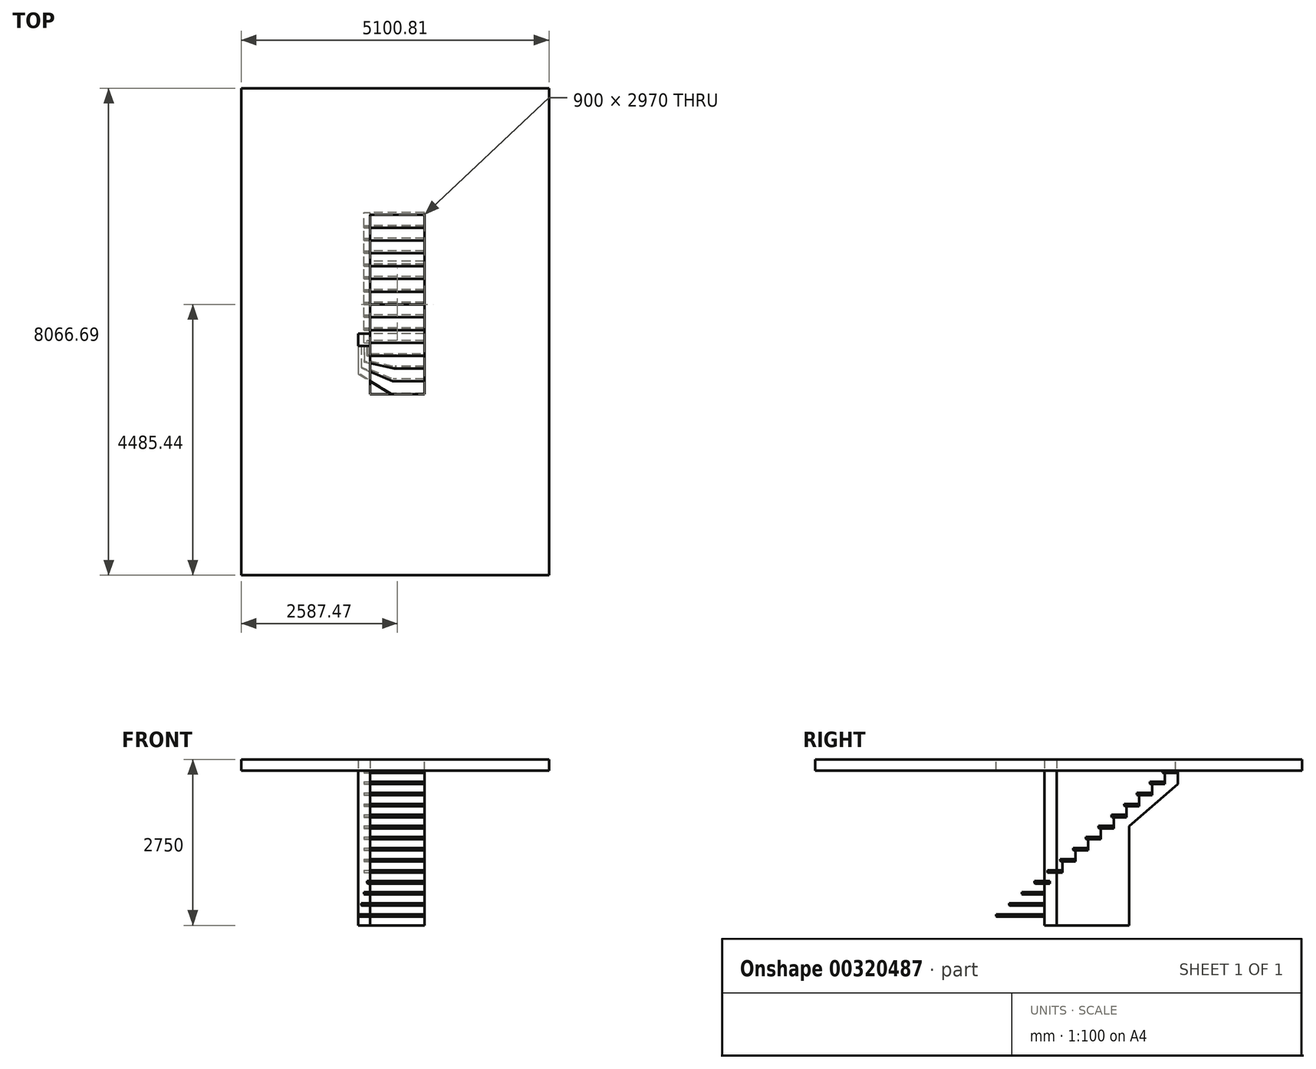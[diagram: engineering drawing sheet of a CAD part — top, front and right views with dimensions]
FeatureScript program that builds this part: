
annotation { "Feature Type Name" : "Feature", "Feature Type Description" : "" }
export const myFeature = defineFeature(function(context is Context, id is Id, definition is map)
    precondition{}
    {
        {
            var Q0;
            Q0=qCreatedBy(makeId("Top.planeOp"),FACE);
            var sketch = newSketch(context, id + "F0", { "sketchPlane" : qUnion([Q0])});
            skLineSegment(sketch, "E0.bottom", {"start": v(0, 2170) * mm, "end": v(-900, 2170) * mm});
            skLineSegment(sketch, "E0.top", {"start": v(0, -800) * mm, "end": v(-900, -800) * mm});
            skLineSegment(sketch, "E0.left", {"start": v(0, 2170) * mm, "end": v(0, -800) * mm});
            skLineSegment(sketch, "E0.right", {"start": v(-900, 2170) * mm, "end": v(-900, -800) * mm});
            skSolve(sketch);
        }
        {
            var Q0;
            Q0=qCreatedBy(makeId("Top.planeOp"),FACE);
            cPlane(context, id + "F1", {"entities" : qUnion([Q0]), "cplaneType" : CPlaneType.OFFSET, "offset" : 2750 * mm, "width" : 150 * mm, "height" : 150 * mm});
        }
        {
            var Q0;
            Q0=qCreatedBy(id+"F1.planeOp",FACE);
            var sketch = newSketch(context, id + "F2", { "sketchPlane" : qUnion([Q0])});
            skLineSegment(sketch, "E1.0", {"start": v(0, 2170) * mm, "end": v(-900, 2170) * mm});
            skLineSegment(sketch, "E1.1", {"start": v(-900, 2170) * mm, "end": v(-900, -800) * mm});
            skLineSegment(sketch, "E1.2", {"start": v(0, -800) * mm, "end": v(-900, -800) * mm});
            skLineSegment(sketch, "E1.3", {"start": v(0, 2170) * mm, "end": v(0, -800) * mm});
            skLineSegment(sketch, "E2.bottom", {"start": v(-3037.47, 4266.25) * mm, "end": v(2063.34, 4266.25) * mm});
            skLineSegment(sketch, "E2.top", {"start": v(-3037.47, -3800.44) * mm, "end": v(2063.34, -3800.44) * mm});
            skLineSegment(sketch, "E2.left", {"start": v(-3037.47, 4266.25) * mm, "end": v(-3037.47, -3800.44) * mm});
            skLineSegment(sketch, "E2.right", {"start": v(2063.34, 4266.25) * mm, "end": v(2063.34, -3800.44) * mm});
            skSolve(sketch);
        }
        {
            var Q0;
            Q0=makeQuery(id+"F2.imprint","IMPRINT",FACE,{"disambiguationData":[TD([[makeQuery(id+"F2.imprint","IMPRINT",EDGE,{"derivedFrom":sQuery(id+"F2.wireOp",EDGE,"E1.0")}),-1.0]])]});
            extrude(context, id + "F3", {"entities" : qUnion([Q0]), "oppositeDirection" : true, "depth" : 188 * mm});
        }
        {
            var Q0;
            Q0=qCreatedBy(makeId("Top.planeOp"),FACE);
            var sketch = newSketch(context, id + "F4", { "sketchPlane" : qUnion([Q0])});
            skPoint(sketch, "E3.0", {"position": v(0, 0) * mm});
            skLineSegment(sketch, "E4.0", {"start": v(-900, 2170) * mm, "end": v(-900, -800) * mm});
            skLineSegment(sketch, "E5.bottom", {"start": v(-900, 0) * mm, "end": v(-1100, 0) * mm});
            skLineSegment(sketch, "E5.top", {"start": v(-900, 200) * mm, "end": v(-1100, 200) * mm});
            skLineSegment(sketch, "E5.left", {"start": v(-900, 0) * mm, "end": v(-900, 200) * mm});
            skLineSegment(sketch, "E5.right", {"start": v(-1100, 0) * mm, "end": v(-1100, 200) * mm});
            skSolve(sketch);
        }
        {
            var Q0;
            Q0=makeQuery(id+"F4.imprint","IMPRINT",FACE,{"disambiguationData":[TD([[makeQuery(id+"F4.imprint","IMPRINT",EDGE,{"derivedFrom":sQuery(id+"F4.wireOp",EDGE,"E5.bottom")}),-1.0]])]});
            var Q1;
            Q1=qCreatedBy(id+"F1.planeOp",FACE);
            extrude(context, id + "F5", {"entities" : qUnion([Q0]), "endBound" : BoundingType.UP_TO_SURFACE, "endBoundEntityFace" : qUnion([Q1]), "depth" : 25 * mm});
        }
        {
            var Q0;
            Q0=qCreatedBy(makeId("Right.planeOp"),FACE);
            var Q1;
            Q1=sQuery(id+"F0.wireOp",VERTEX,"E0.right.end");
            cPlane(context, id + "F6", {"entities" : qUnion([Q0, Q1]), "cplaneType" : CPlaneType.PLANE_POINT, "offset" : 25 * mm, "width" : 150 * mm, "height" : 150 * mm});
        }
        {
            var Q0;
            Q0=qCreatedBy(id+"F6.planeOp",FACE);
            var sketch = newSketch(context, id + "F7", { "sketchPlane" : qUnion([Q0])});
            skLineSegment(sketch, "E6", {"start": v(-800, 0) * mm, "end": v(-800, 183) * mm});
            skLineSegment(sketch, "E7", {"start": v(-800, 183) * mm, "end": v(-588, 183) * mm});
            skLineSegment(sketch, "E8", {"start": v(-588, 183) * mm, "end": v(-588, 366) * mm});
            skLineSegment(sketch, "E9", {"start": v(-588, 366) * mm, "end": v(-376, 366) * mm});
            skLineSegment(sketch, "E10", {"start": v(-376, 366) * mm, "end": v(-376, 549) * mm});
            skLineSegment(sketch, "E11", {"start": v(-376, 549) * mm, "end": v(-164, 549) * mm});
            skLineSegment(sketch, "E12", {"start": v(-164, 549) * mm, "end": v(-164, 732) * mm});
            skLineSegment(sketch, "E13", {"start": v(-164, 732) * mm, "end": v(48, 732) * mm});
            skLineSegment(sketch, "E14", {"start": v(48, 732) * mm, "end": v(48, 915) * mm});
            skLineSegment(sketch, "E15", {"start": v(48, 915) * mm, "end": v(260, 915) * mm});
            skLineSegment(sketch, "E16", {"start": v(260, 915) * mm, "end": v(260, 1098) * mm});
            skLineSegment(sketch, "E17", {"start": v(260, 1098) * mm, "end": v(472, 1098) * mm});
            skLineSegment(sketch, "E18", {"start": v(472, 1098) * mm, "end": v(472, 1281) * mm});
            skLineSegment(sketch, "E19", {"start": v(472, 1281) * mm, "end": v(684, 1281) * mm});
            skLineSegment(sketch, "E20", {"start": v(684, 1281) * mm, "end": v(684, 1464) * mm});
            skLineSegment(sketch, "E21", {"start": v(684, 1464) * mm, "end": v(896, 1464) * mm});
            skLineSegment(sketch, "E22", {"start": v(896, 1464) * mm, "end": v(896, 1647) * mm});
            skLineSegment(sketch, "E23", {"start": v(896, 1647) * mm, "end": v(1108, 1647) * mm});
            skPoint(sketch, "E24.0", {"position": v(2170, 2750) * mm});
            skLineSegment(sketch, "E25", {"start": v(1108, 1647) * mm, "end": v(1108, 1830) * mm});
            skLineSegment(sketch, "E26", {"start": v(1108, 1830) * mm, "end": v(1320, 1830) * mm});
            skLineSegment(sketch, "E27", {"start": v(1320, 1830) * mm, "end": v(1320, 2013) * mm});
            skLineSegment(sketch, "E28", {"start": v(1320, 2013) * mm, "end": v(1532, 2013) * mm});
            skLineSegment(sketch, "E29", {"start": v(1532, 2013) * mm, "end": v(1532, 2196) * mm});
            skLineSegment(sketch, "E30", {"start": v(1532, 2196) * mm, "end": v(1744, 2196) * mm});
            skLineSegment(sketch, "E31", {"start": v(1744, 2196) * mm, "end": v(1744, 2379) * mm});
            skLineSegment(sketch, "E32", {"start": v(1744, 2379) * mm, "end": v(1956, 2379) * mm});
            skLineSegment(sketch, "E33", {"start": v(1956, 2379) * mm, "end": v(1956, 2562) * mm});
            skLineSegment(sketch, "E34", {"start": v(1956, 2562) * mm, "end": v(2168, 2562) * mm});
            skLineSegment(sketch, "E35", {"start": v(2168, 2562) * mm, "end": v(2168, 2745) * mm});
            skLineSegment(sketch, "E36", {"start": v(2168, 2745) * mm, "end": v(2380, 2745) * mm});
            skSolve(sketch);
        }
        {
            var Q0;
            Q0=qCreatedBy(id+"F6.planeOp",FACE);
            var sketch = newSketch(context, id + "F8", { "sketchPlane" : qUnion([Q0])});
            skLineSegment(sketch, "E37.0", {"start": v(2168, 2745) * mm, "end": v(2380, 2745) * mm});
            skLineSegment(sketch, "E37.1", {"start": v(1956, 2562) * mm, "end": v(2168, 2562) * mm});
            skLineSegment(sketch, "E37.2", {"start": v(1744, 2379) * mm, "end": v(1956, 2379) * mm});
            skLineSegment(sketch, "E37.3", {"start": v(1532, 2196) * mm, "end": v(1744, 2196) * mm});
            skLineSegment(sketch, "E37.4", {"start": v(1320, 2013) * mm, "end": v(1532, 2013) * mm});
            skLineSegment(sketch, "E37.5", {"start": v(1108, 1830) * mm, "end": v(1320, 1830) * mm});
            skLineSegment(sketch, "E37.6", {"start": v(896, 1647) * mm, "end": v(1108, 1647) * mm});
            skLineSegment(sketch, "E37.7", {"start": v(684, 1464) * mm, "end": v(896, 1464) * mm});
            skLineSegment(sketch, "E37.8", {"start": v(472, 1281) * mm, "end": v(684, 1281) * mm});
            skLineSegment(sketch, "E37.9", {"start": v(260, 1098) * mm, "end": v(472, 1098) * mm});
            skLineSegment(sketch, "E37.10", {"start": v(48, 915) * mm, "end": v(260, 915) * mm});
            skLineSegment(sketch, "E38.bottom", {"start": v(1956, 2562) * mm, "end": v(2206, 2562) * mm});
            skLineSegment(sketch, "E38.top", {"start": v(1956, 2522) * mm, "end": v(2206, 2522) * mm});
            skLineSegment(sketch, "E38.left", {"start": v(1956, 2562) * mm, "end": v(1956, 2522) * mm});
            skLineSegment(sketch, "E38.right", {"start": v(2206, 2562) * mm, "end": v(2206, 2522) * mm});
            skLineSegment(sketch, "E39.bottom", {"start": v(1744, 2379) * mm, "end": v(1994, 2379) * mm});
            skLineSegment(sketch, "E39.top", {"start": v(1744, 2339) * mm, "end": v(1994, 2339) * mm});
            skLineSegment(sketch, "E39.left", {"start": v(1744, 2379) * mm, "end": v(1744, 2339) * mm});
            skLineSegment(sketch, "E39.right", {"start": v(1994, 2379) * mm, "end": v(1994, 2339) * mm});
            skLineSegment(sketch, "E40.bottom", {"start": v(1532, 2196) * mm, "end": v(1782, 2196) * mm});
            skLineSegment(sketch, "E40.top", {"start": v(1532, 2156) * mm, "end": v(1782, 2156) * mm});
            skLineSegment(sketch, "E40.left", {"start": v(1532, 2196) * mm, "end": v(1532, 2156) * mm});
            skLineSegment(sketch, "E40.right", {"start": v(1782, 2196) * mm, "end": v(1782, 2156) * mm});
            skLineSegment(sketch, "E41.bottom", {"start": v(1320, 2013) * mm, "end": v(1570, 2013) * mm});
            skLineSegment(sketch, "E41.top", {"start": v(1320, 1973) * mm, "end": v(1570, 1973) * mm});
            skLineSegment(sketch, "E41.left", {"start": v(1320, 2013) * mm, "end": v(1320, 1973) * mm});
            skLineSegment(sketch, "E41.right", {"start": v(1570, 2013) * mm, "end": v(1570, 1973) * mm});
            skLineSegment(sketch, "E42.bottom", {"start": v(1108, 1830) * mm, "end": v(1358, 1830) * mm});
            skLineSegment(sketch, "E42.top", {"start": v(1108, 1790) * mm, "end": v(1358, 1790) * mm});
            skLineSegment(sketch, "E42.left", {"start": v(1108, 1830) * mm, "end": v(1108, 1790) * mm});
            skLineSegment(sketch, "E42.right", {"start": v(1358, 1830) * mm, "end": v(1358, 1790) * mm});
            skLineSegment(sketch, "E43.bottom", {"start": v(896, 1647) * mm, "end": v(1146, 1647) * mm});
            skLineSegment(sketch, "E43.top", {"start": v(896, 1607) * mm, "end": v(1146, 1607) * mm});
            skLineSegment(sketch, "E43.left", {"start": v(896, 1647) * mm, "end": v(896, 1607) * mm});
            skLineSegment(sketch, "E43.right", {"start": v(1146, 1647) * mm, "end": v(1146, 1607) * mm});
            skLineSegment(sketch, "E44.bottom", {"start": v(684, 1464) * mm, "end": v(934, 1464) * mm});
            skLineSegment(sketch, "E44.top", {"start": v(684, 1424) * mm, "end": v(934, 1424) * mm});
            skLineSegment(sketch, "E44.left", {"start": v(684, 1464) * mm, "end": v(684, 1424) * mm});
            skLineSegment(sketch, "E44.right", {"start": v(934, 1464) * mm, "end": v(934, 1424) * mm});
            skLineSegment(sketch, "E45.bottom", {"start": v(472, 1281) * mm, "end": v(722, 1281) * mm});
            skLineSegment(sketch, "E45.top", {"start": v(472, 1241) * mm, "end": v(722, 1241) * mm});
            skLineSegment(sketch, "E45.left", {"start": v(472, 1281) * mm, "end": v(472, 1241) * mm});
            skLineSegment(sketch, "E45.right", {"start": v(722, 1281) * mm, "end": v(722, 1241) * mm});
            skLineSegment(sketch, "E46.bottom", {"start": v(260, 1098) * mm, "end": v(510, 1098) * mm});
            skLineSegment(sketch, "E46.top", {"start": v(260, 1058) * mm, "end": v(510, 1058) * mm});
            skLineSegment(sketch, "E46.left", {"start": v(260, 1098) * mm, "end": v(260, 1058) * mm});
            skLineSegment(sketch, "E46.right", {"start": v(510, 1098) * mm, "end": v(510, 1058) * mm});
            skLineSegment(sketch, "E47.bottom", {"start": v(48, 915) * mm, "end": v(298, 915) * mm});
            skLineSegment(sketch, "E47.top", {"start": v(48, 875) * mm, "end": v(298, 875) * mm});
            skLineSegment(sketch, "E47.left", {"start": v(48, 915) * mm, "end": v(48, 875) * mm});
            skLineSegment(sketch, "E47.right", {"start": v(298, 915) * mm, "end": v(298, 875) * mm});
            skLineSegment(sketch, "E48.0", {"start": v(-164, 732) * mm, "end": v(48, 732) * mm});
            skLineSegment(sketch, "E49.bottom", {"start": v(-164, 732) * mm, "end": v(86, 732) * mm});
            skLineSegment(sketch, "E49.top", {"start": v(-164, 692) * mm, "end": v(86, 692) * mm});
            skLineSegment(sketch, "E49.left", {"start": v(-164, 732) * mm, "end": v(-164, 692) * mm});
            skLineSegment(sketch, "E49.right", {"start": v(86, 732) * mm, "end": v(86, 692) * mm});
            skSolve(sketch);
        }
        {
            var Q0;
            Q0=makeQuery(id+"F8.imprint","IMPRINT",FACE,{"disambiguationData":[TD([[makeQuery(id+"F8.imprint","IMPRINT",EDGE,{"derivedFrom":sQuery(id+"F8.wireOp",EDGE,"E38.top")}),1.0]])]});
            var Q1;
            Q1=makeQuery(id+"F8.imprint","IMPRINT",FACE,{"disambiguationData":[TD([[makeQuery(id+"F8.imprint","IMPRINT",EDGE,{"derivedFrom":sQuery(id+"F8.wireOp",EDGE,"E39.top")}),1.0]])]});
            var Q2;
            Q2=makeQuery(id+"F8.imprint","IMPRINT",FACE,{"disambiguationData":[TD([[makeQuery(id+"F8.imprint","IMPRINT",EDGE,{"derivedFrom":sQuery(id+"F8.wireOp",EDGE,"E40.top")}),1.0]])]});
            var Q3;
            Q3=makeQuery(id+"F8.imprint","IMPRINT",FACE,{"disambiguationData":[TD([[makeQuery(id+"F8.imprint","IMPRINT",EDGE,{"derivedFrom":sQuery(id+"F8.wireOp",EDGE,"E41.top")}),1.0]])]});
            var Q4;
            Q4=makeQuery(id+"F8.imprint","IMPRINT",FACE,{"disambiguationData":[TD([[makeQuery(id+"F8.imprint","IMPRINT",EDGE,{"derivedFrom":sQuery(id+"F8.wireOp",EDGE,"E42.top")}),1.0]])]});
            var Q5;
            Q5=makeQuery(id+"F8.imprint","IMPRINT",FACE,{"disambiguationData":[TD([[makeQuery(id+"F8.imprint","IMPRINT",EDGE,{"derivedFrom":sQuery(id+"F8.wireOp",EDGE,"E43.top")}),1.0]])]});
            var Q6;
            Q6=makeQuery(id+"F8.imprint","IMPRINT",FACE,{"disambiguationData":[TD([[makeQuery(id+"F8.imprint","IMPRINT",EDGE,{"derivedFrom":sQuery(id+"F8.wireOp",EDGE,"E44.top")}),1.0]])]});
            var Q7;
            Q7=makeQuery(id+"F8.imprint","IMPRINT",FACE,{"disambiguationData":[TD([[makeQuery(id+"F8.imprint","IMPRINT",EDGE,{"derivedFrom":sQuery(id+"F8.wireOp",EDGE,"E45.top")}),1.0]])]});
            var Q8;
            Q8=makeQuery(id+"F8.imprint","IMPRINT",FACE,{"disambiguationData":[TD([[makeQuery(id+"F8.imprint","IMPRINT",EDGE,{"derivedFrom":sQuery(id+"F8.wireOp",EDGE,"E46.top")}),1.0]])]});
            var Q9;
            Q9=makeQuery(id+"F8.imprint","IMPRINT",FACE,{"disambiguationData":[TD([[makeQuery(id+"F8.imprint","IMPRINT",EDGE,{"derivedFrom":sQuery(id+"F8.wireOp",EDGE,"E47.top")}),1.0]])]});
            var Q10;
            Q10=makeQuery(id+"F8.imprint","IMPRINT",FACE,{"disambiguationData":[TD([[makeQuery(id+"F8.imprint","IMPRINT",EDGE,{"derivedFrom":sQuery(id+"F8.wireOp",EDGE,"E49.top")}),1.0]])]});
            var Q11;
            Q11=qCreatedBy(makeId("Right.planeOp"),FACE);
            extrude(context, id + "F9", {"entities" : qUnion([Q0, Q1, Q2, Q3, Q4, Q5, Q6, Q7, Q8, Q9, Q10]), "endBound" : BoundingType.UP_TO_SURFACE, "endBoundEntityFace" : qUnion([Q11]), "depth" : 25 * mm});
        }
        {
            var Q0;
            Q0=makeQuery(id+"F9.opExtrude","CAP_FACE",FACE,{"disambiguationData":[OSD([sQuery(id+"F8.wireOp",EDGE,"E38.bottom"),sQuery(id+"F8.wireOp",EDGE,"E38.top"),sQuery(id+"F8.wireOp",EDGE,"E38.left"),sQuery(id+"F8.wireOp",EDGE,"E38.right")])],"isStart":true});
            var Q1;
            Q1=makeQuery(id+"F9.opExtrude","CAP_FACE",FACE,{"disambiguationData":[OSD([sQuery(id+"F8.wireOp",EDGE,"E39.bottom"),sQuery(id+"F8.wireOp",EDGE,"E39.top"),sQuery(id+"F8.wireOp",EDGE,"E39.left"),sQuery(id+"F8.wireOp",EDGE,"E39.right")])],"isStart":true});
            var Q2;
            Q2=makeQuery(id+"F9.opExtrude","CAP_FACE",FACE,{"disambiguationData":[OSD([sQuery(id+"F8.wireOp",EDGE,"E40.bottom"),sQuery(id+"F8.wireOp",EDGE,"E40.top"),sQuery(id+"F8.wireOp",EDGE,"E40.left"),sQuery(id+"F8.wireOp",EDGE,"E40.right")])],"isStart":true});
            var Q3;
            Q3=makeQuery(id+"F9.opExtrude","CAP_FACE",FACE,{"disambiguationData":[OSD([sQuery(id+"F8.wireOp",EDGE,"E41.bottom"),sQuery(id+"F8.wireOp",EDGE,"E41.top"),sQuery(id+"F8.wireOp",EDGE,"E41.left"),sQuery(id+"F8.wireOp",EDGE,"E41.right")])],"isStart":true});
            var Q4;
            Q4=makeQuery(id+"F9.opExtrude","CAP_FACE",FACE,{"disambiguationData":[OSD([sQuery(id+"F8.wireOp",EDGE,"E42.bottom"),sQuery(id+"F8.wireOp",EDGE,"E42.top"),sQuery(id+"F8.wireOp",EDGE,"E42.left"),sQuery(id+"F8.wireOp",EDGE,"E42.right")])],"isStart":true});
            var Q5;
            Q5=makeQuery(id+"F9.opExtrude","CAP_FACE",FACE,{"disambiguationData":[OSD([sQuery(id+"F8.wireOp",EDGE,"E43.bottom"),sQuery(id+"F8.wireOp",EDGE,"E43.top"),sQuery(id+"F8.wireOp",EDGE,"E43.left"),sQuery(id+"F8.wireOp",EDGE,"E43.right")])],"isStart":true});
            var Q6;
            Q6=makeQuery(id+"F9.opExtrude","CAP_FACE",FACE,{"disambiguationData":[OSD([sQuery(id+"F8.wireOp",EDGE,"E44.bottom"),sQuery(id+"F8.wireOp",EDGE,"E44.top"),sQuery(id+"F8.wireOp",EDGE,"E44.left"),sQuery(id+"F8.wireOp",EDGE,"E44.right")])],"isStart":true});
            var Q7;
            Q7=makeQuery(id+"F9.opExtrude","CAP_FACE",FACE,{"disambiguationData":[OSD([sQuery(id+"F8.wireOp",EDGE,"E45.bottom"),sQuery(id+"F8.wireOp",EDGE,"E45.top"),sQuery(id+"F8.wireOp",EDGE,"E45.left"),sQuery(id+"F8.wireOp",EDGE,"E45.right")])],"isStart":true});
            var Q8;
            Q8=makeQuery(id+"F9.opExtrude","CAP_FACE",FACE,{"disambiguationData":[OSD([sQuery(id+"F8.wireOp",EDGE,"E46.bottom"),sQuery(id+"F8.wireOp",EDGE,"E46.top"),sQuery(id+"F8.wireOp",EDGE,"E46.left"),sQuery(id+"F8.wireOp",EDGE,"E46.right")])],"isStart":true});
            var Q9;
            Q9=makeQuery(id+"F9.opExtrude","CAP_FACE",FACE,{"disambiguationData":[OSD([sQuery(id+"F8.wireOp",EDGE,"E47.bottom"),sQuery(id+"F8.wireOp",EDGE,"E47.top"),sQuery(id+"F8.wireOp",EDGE,"E47.left"),sQuery(id+"F8.wireOp",EDGE,"E47.right")])],"isStart":true});
            extrude(context, id + "F10", {"entities" : qUnion([Q0, Q1, Q2, Q3, Q4, Q5, Q6, Q7, Q8, Q9]), "depth" : 100 * mm});
        }
        {
            var Q0;
            Q0=qCreatedBy(id+"F6.planeOp",FACE);
            var sketch = newSketch(context, id + "F11", { "sketchPlane" : qUnion([Q0])});
            skLineSegment(sketch, "E50.0", {"start": v(298, 915) * mm, "end": v(298, 875) * mm});
            skLineSegment(sketch, "E50.1", {"start": v(510, 1098) * mm, "end": v(510, 1058) * mm});
            skLineSegment(sketch, "E50.2", {"start": v(722, 1281) * mm, "end": v(722, 1241) * mm});
            skLineSegment(sketch, "E50.3", {"start": v(934, 1464) * mm, "end": v(934, 1424) * mm});
            skLineSegment(sketch, "E50.4", {"start": v(1146, 1647) * mm, "end": v(1146, 1607) * mm});
            skLineSegment(sketch, "E50.5", {"start": v(1358, 1830) * mm, "end": v(1358, 1790) * mm});
            skLineSegment(sketch, "E50.6", {"start": v(1570, 2013) * mm, "end": v(1570, 1973) * mm});
            skLineSegment(sketch, "E50.7", {"start": v(1782, 2196) * mm, "end": v(1782, 2156) * mm});
            skLineSegment(sketch, "E50.8", {"start": v(1994, 2379) * mm, "end": v(1994, 2339) * mm});
            skLineSegment(sketch, "E50.9", {"start": v(2206, 2562) * mm, "end": v(2206, 2522) * mm});
            skLineSegment(sketch, "E51", {"start": v(298, 915) * mm, "end": v(298, 1058) * mm});
            skLineSegment(sketch, "E52", {"start": v(298, 1058) * mm, "end": v(510, 1058) * mm});
            skLineSegment(sketch, "E53", {"start": v(510, 1098) * mm, "end": v(510, 1241) * mm});
            skLineSegment(sketch, "E54", {"start": v(510, 1241) * mm, "end": v(722, 1241) * mm});
            skLineSegment(sketch, "E55", {"start": v(722, 1281) * mm, "end": v(722, 1424) * mm});
            skLineSegment(sketch, "E56", {"start": v(722, 1424) * mm, "end": v(934, 1424) * mm});
            skLineSegment(sketch, "E57", {"start": v(934, 1464) * mm, "end": v(934, 1607) * mm});
            skLineSegment(sketch, "E58", {"start": v(934, 1607) * mm, "end": v(1146, 1607) * mm});
            skLineSegment(sketch, "E59", {"start": v(1146, 1647) * mm, "end": v(1146, 1790) * mm});
            skLineSegment(sketch, "E60", {"start": v(1146, 1790) * mm, "end": v(1358, 1790) * mm});
            skLineSegment(sketch, "E61", {"start": v(1358, 1830) * mm, "end": v(1358, 1973) * mm});
            skLineSegment(sketch, "E62", {"start": v(1358, 1973) * mm, "end": v(1570, 1973) * mm});
            skLineSegment(sketch, "E63", {"start": v(1570, 2013) * mm, "end": v(1570, 2156) * mm});
            skLineSegment(sketch, "E64", {"start": v(1570, 2156) * mm, "end": v(1782, 2156) * mm});
            skLineSegment(sketch, "E65", {"start": v(1782, 2196) * mm, "end": v(1782, 2339) * mm});
            skLineSegment(sketch, "E66", {"start": v(1782, 2339) * mm, "end": v(1994, 2339) * mm});
            skLineSegment(sketch, "E67", {"start": v(1994, 2379) * mm, "end": v(1994, 2522) * mm});
            skLineSegment(sketch, "E68", {"start": v(1994, 2522) * mm, "end": v(2206, 2522) * mm});
            skPoint(sketch, "E69.0", {"position": v(200, 875) * mm});
            skLineSegment(sketch, "E70", {"start": v(298, 875) * mm, "end": v(200, 875) * mm});
            skLineSegment(sketch, "E71", {"start": v(200, 0) * mm, "end": v(1400, 0) * mm});
            skLineSegment(sketch, "E72", {"start": v(1400, 0) * mm, "end": v(1400, 1973) * mm});
            skLineSegment(sketch, "E73", {"start": v(200, 875) * mm, "end": v(200, 0) * mm});
            skLineSegment(sketch, "E74", {"start": v(2206, 2522) * mm, "end": v(2206, 2339) * mm});
            skLineSegment(sketch, "E75", {"start": v(1146, 1607) * mm, "end": v(1146, 1424) * mm});
            skLineSegment(sketch, "E76", {"start": v(1146, 1424) * mm, "end": v(2206, 2339) * mm});
            skSolve(sketch);
        }
        {
            var Q0;
            Q0=makeQuery(id+"F11.imprint","IMPRINT",FACE,{"disambiguationData":[TD([[makeQuery(id+"F11.imprint","IMPRINT",EDGE,{"derivedFrom":sQuery(id+"F11.wireOp",EDGE,"E50.0")}),1.0]])]});
            var Q1;
            Q1=makeQuery(id+"F11.imprint","IMPRINT",FACE,{"disambiguationData":[TD([[makeQuery(id+"F11.imprint","IMPRINT",EDGE,{"derivedFrom":sQuery(id+"F11.wireOp",EDGE,"E50.4")}),1.0]])]});
            var Q2;
            {var subQ0=sQuery(id+"F11.wireOp",EDGE,"E50.6");Q2=makeQuery(id+"F11.imprint","IMPRINT",FACE,{"disambiguationData":[TD([[makeQuery(id+"F11.imprint","IMPRINT",EDGE,{"derivedFrom":subQ0}),1.0]])]});}
            var Q3;
            Q3=qCreatedBy(makeId("Right.planeOp"),FACE);
            extrude(context, id + "F12", {"entities" : qUnion([Q0, Q1, Q2]), "endBound" : BoundingType.UP_TO_SURFACE, "endBoundEntityFace" : qUnion([Q3]), "depth" : 25 * mm});
        }
        {
            var Q0;
            Q0=makeQuery(id+"F9.opExtrude","CAP_FACE",FACE,{"disambiguationData":[OSD([sQuery(id+"F8.wireOp",EDGE,"E49.bottom"),sQuery(id+"F8.wireOp",EDGE,"E49.top"),sQuery(id+"F8.wireOp",EDGE,"E49.left"),sQuery(id+"F8.wireOp",EDGE,"E49.right")])],"isStart":true});
            extrude(context, id + "F13", {"entities" : qUnion([Q0]), "depth" : 50 * mm});
        }
        {
            var Q0;
            Q0=qCreatedBy(makeId("Top.planeOp"),FACE);
            var Q1;
            Q1=sQuery(id+"F7.wireOp",VERTEX,"E11.start");
            cPlane(context, id + "F14", {"entities" : qUnion([Q0, Q1]), "cplaneType" : CPlaneType.PLANE_POINT, "offset" : 25 * mm, "width" : 150 * mm, "height" : 150 * mm});
        }
        {
            var Q0;
            Q0=qCreatedBy(makeId("Top.planeOp"),FACE);
            var Q1;
            Q1=sQuery(id+"F7.wireOp",VERTEX,"E9.start");
            cPlane(context, id + "F15", {"entities" : qUnion([Q0, Q1]), "cplaneType" : CPlaneType.PLANE_POINT, "offset" : 25 * mm, "width" : 150 * mm, "height" : 150 * mm});
        }
        {
            var Q0;
            Q0=qCreatedBy(makeId("Top.planeOp"),FACE);
            var Q1;
            Q1=sQuery(id+"F7.wireOp",VERTEX,"E7.start");
            cPlane(context, id + "F16", {"entities" : qUnion([Q0, Q1]), "cplaneType" : CPlaneType.PLANE_POINT, "offset" : 25 * mm, "width" : 150 * mm, "height" : 150 * mm});
        }
        {
            var Q0;
            Q0=qCreatedBy(id+"F14.planeOp",FACE);
            var sketch = newSketch(context, id + "F17", { "sketchPlane" : qUnion([Q0])});
            skPoint(sketch, "E77.0", {"position": v(-900, -376) * mm});
            skLineSegment(sketch, "E78.bottom", {"start": v(-500, -376) * mm, "end": v(0, -376) * mm});
            skLineSegment(sketch, "E78.top", {"start": v(-900, -126) * mm, "end": v(0, -126) * mm});
            skLineSegment(sketch, "E78.right", {"start": v(0, -376) * mm, "end": v(0, -126) * mm});
            skLineSegment(sketch, "E79", {"start": v(-1000, -126) * mm, "end": v(-1000, -266) * mm});
            skLineSegment(sketch, "E80", {"start": v(-1000, -266) * mm, "end": v(-500, -376) * mm});
            skLineSegment(sketch, "E81.0", {"start": v(-900, 0) * mm, "end": v(-1000, 0) * mm});
            skLineSegment(sketch, "E82", {"start": v(-900, -126) * mm, "end": v(-900, 0) * mm});
            skLineSegment(sketch, "E83", {"start": v(-1000, -126) * mm, "end": v(-1000, 0) * mm});
            skPoint(sketch, "E84.orphan", {"position": v(-1100, 0) * mm});
            skSolve(sketch);
        }
        {
            var Q0;
            Q0=makeQuery(id+"F17.imprint","IMPRINT",FACE,{"disambiguationData":[TD([[makeQuery(id+"F17.imprint","IMPRINT",EDGE,{"derivedFrom":sQuery(id+"F17.wireOp",EDGE,"E78.bottom")}),1.0]])]});
            extrude(context, id + "F18", {"entities" : qUnion([Q0]), "oppositeDirection" : true, "depth" : 40 * mm});
        }
        {
            var Q0;
            Q0=qCreatedBy(id+"F15.planeOp",FACE);
            var sketch = newSketch(context, id + "F19", { "sketchPlane" : qUnion([Q0])});
            skPoint(sketch, "E85.0", {"position": v(-900, -588) * mm});
            skLineSegment(sketch, "E86", {"start": v(-525, -588) * mm, "end": v(0, -588) * mm});
            skLineSegment(sketch, "E87", {"start": v(0, -588) * mm, "end": v(0, -338) * mm});
            skPoint(sketch, "E88", {"position": v(-525, -588) * mm});
            skPoint(sketch, "E89", {"position": v(-1000, -226) * mm});
            skLineSegment(sketch, "E90", {"start": v(0, -338) * mm, "end": v(-490.9, -338) * mm});
            skLineSegment(sketch, "E91", {"start": v(-900, -248) * mm, "end": v(-490.9, -338) * mm});
            skPoint(sketch, "E92.orphan", {"position": v(-1000, -266) * mm});
            skLineSegment(sketch, "E93", {"start": v(-1050, -226) * mm, "end": v(-1050, -366) * mm});
            skLineSegment(sketch, "E94", {"start": v(-1050, -366) * mm, "end": v(-525, -588) * mm});
            skLineSegment(sketch, "E95.0", {"start": v(-900, 0) * mm, "end": v(-1050, 0) * mm});
            skLineSegment(sketch, "E96", {"start": v(-900, 0) * mm, "end": v(-900, -248) * mm});
            skLineSegment(sketch, "E97", {"start": v(-1050, -226) * mm, "end": v(-1050, 0) * mm});
            skPoint(sketch, "E98.orphan", {"position": v(-1100, 0) * mm});
            skSolve(sketch);
        }
        {
            var Q0;
            Q0=makeQuery(id+"F19.imprint","IMPRINT",FACE,{"disambiguationData":[TD([[makeQuery(id+"F19.imprint","IMPRINT",EDGE,{"derivedFrom":sQuery(id+"F19.wireOp",EDGE,"E86")}),1.0]])]});
            extrude(context, id + "F20", {"entities" : qUnion([Q0]), "oppositeDirection" : true, "depth" : 40 * mm});
        }
        {
            var Q0;
            Q0=qCreatedBy(id+"F16.planeOp",FACE);
            var sketch = newSketch(context, id + "F21", { "sketchPlane" : qUnion([Q0])});
            skPoint(sketch, "E99.0", {"position": v(-900, -800) * mm});
            skLineSegment(sketch, "E100", {"start": v(-550, -800) * mm, "end": v(0, -800) * mm});
            skLineSegment(sketch, "E101", {"start": v(0, -800) * mm, "end": v(0, -550) * mm});
            skLineSegment(sketch, "E102", {"start": v(0, -550) * mm, "end": v(-520.27, -550) * mm});
            skPoint(sketch, "E103", {"position": v(-550, -800) * mm});
            skPoint(sketch, "E104", {"position": v(-1050, -326) * mm});
            skLineSegment(sketch, "E105", {"start": v(-900, -389.43) * mm, "end": v(-520.27, -550) * mm});
            skLineSegment(sketch, "E106.0", {"start": v(-900, 0) * mm, "end": v(-1100, 0) * mm});
            skLineSegment(sketch, "E107", {"start": v(-900, 0) * mm, "end": v(-900, -389.43) * mm});
            skLineSegment(sketch, "E108", {"start": v(-900, -389.43) * mm, "end": v(-900, 0) * mm});
            skLineSegment(sketch, "E109", {"start": v(-1100, -326) * mm, "end": v(-1100, -466) * mm});
            skPoint(sketch, "E110.orphan", {"position": v(-1050, -366) * mm});
            skPoint(sketch, "E111.0.end.orphan", {"position": v(-1050, 0) * mm});
            skLineSegment(sketch, "E112", {"start": v(-1100, 0) * mm, "end": v(-1100, -326) * mm});
            skLineSegment(sketch, "E113", {"start": v(-1100, -466) * mm, "end": v(-550, -800) * mm});
            skSolve(sketch);
        }
        {
            var Q0;
            Q0=makeQuery(id+"F21.imprint","IMPRINT",FACE,{"disambiguationData":[TD([[makeQuery(id+"F21.imprint","IMPRINT",EDGE,{"derivedFrom":sQuery(id+"F21.wireOp",EDGE,"E100")}),1.0]])]});
            extrude(context, id + "F22", {"entities" : qUnion([Q0]), "oppositeDirection" : true, "depth" : 40 * mm});
        }
        {
            var Q0;
            Q0=makeQuery(id+"F22.opExtrude","CAP_FACE",FACE,{"disambiguationData":[OSD([sQuery(id+"F21.wireOp",EDGE,"E100"),sQuery(id+"F21.wireOp",EDGE,"E101"),sQuery(id+"F21.wireOp",EDGE,"E102"),sQuery(id+"F21.wireOp",EDGE,"E105"),sQuery(id+"F21.wireOp",EDGE,"E106.0"),sQuery(id+"F21.wireOp",EDGE,"E108"),sQuery(id+"F21.wireOp",EDGE,"E109"),sQuery(id+"F21.wireOp",EDGE,"E112"),sQuery(id+"F21.wireOp",EDGE,"E113")])],"isStart":false});
            var sketch = newSketch(context, id + "F23", { "sketchPlane" : qUnion([Q0])});
            skLineSegment(sketch, "E114.0", {"start": v(-538.8, 760) * mm, "end": v(0, 760) * mm});
            skLineSegment(sketch, "E114.1", {"start": v(-1060, 443.5) * mm, "end": v(-538.8, 760) * mm});
            skLineSegment(sketch, "E114.2", {"start": v(-1060, 0) * mm, "end": v(-1060, 443.5) * mm});
            skSolve(sketch);
        }
        {
            var Q0;
            Q0=sQuery(id+"F23.wireOp",EDGE,"E114.2");
            var Q1;
            Q1=sQuery(id+"F23.wireOp",EDGE,"E114.1");
            var Q2;
            Q2=sQuery(id+"F23.wireOp",EDGE,"E114.0");
            var Q3;
            Q3=makeQuery(id+"F5.opExtrude","CAP_FACE",FACE,{"disambiguationData":[OSD([sQuery(id+"F4.wireOp",EDGE,"E5.bottom"),sQuery(id+"F4.wireOp",EDGE,"E5.top"),sQuery(id+"F4.wireOp",EDGE,"E5.left"),sQuery(id+"F4.wireOp",EDGE,"E5.right")])],"isStart":true});
            extrude(context, id + "F24", {"bodyType" : ToolBodyType.SURFACE, "surfaceEntities" : qUnion([Q0, Q1, Q2]), "endBound" : BoundingType.UP_TO_SURFACE, "endBoundEntityFace" : qUnion([Q3]), "depth" : 25 * mm});
        }
        {
            var Q0;
            Q0=makeQuery(id+"F20.opExtrude","CAP_FACE",FACE,{"disambiguationData":[OSD([sQuery(id+"F19.wireOp",EDGE,"E86"),sQuery(id+"F19.wireOp",EDGE,"E87"),sQuery(id+"F19.wireOp",EDGE,"E90"),sQuery(id+"F19.wireOp",EDGE,"E91"),sQuery(id+"F19.wireOp",EDGE,"E93"),sQuery(id+"F19.wireOp",EDGE,"E94"),sQuery(id+"F19.wireOp",EDGE,"E95.0"),sQuery(id+"F19.wireOp",EDGE,"E96"),sQuery(id+"F19.wireOp",EDGE,"E97")])],"isStart":false});
            var sketch = newSketch(context, id + "F25", { "sketchPlane" : qUnion([Q0])});
            skLineSegment(sketch, "E115.0", {"start": v(-1010, 339.49) * mm, "end": v(-1010, 0) * mm});
            skLineSegment(sketch, "E115.1", {"start": v(-1010, 339.49) * mm, "end": v(-516.9, 548) * mm});
            skLineSegment(sketch, "E115.2", {"start": v(-516.9, 548) * mm, "end": v(0, 548) * mm});
            skSolve(sketch);
        }
        {
            var Q0;
            Q0=sQuery(id+"F25.wireOp",EDGE,"E115.0");
            var Q1;
            Q1=sQuery(id+"F25.wireOp",EDGE,"E115.1");
            var Q2;
            Q2=sQuery(id+"F25.wireOp",EDGE,"E115.2");
            var Q3;
            Q3=makeQuery(id+"F22.opExtrude","CAP_FACE",FACE,{"disambiguationData":[OSD([sQuery(id+"F21.wireOp",EDGE,"E100"),sQuery(id+"F21.wireOp",EDGE,"E101"),sQuery(id+"F21.wireOp",EDGE,"E102"),sQuery(id+"F21.wireOp",EDGE,"E105"),sQuery(id+"F21.wireOp",EDGE,"E106.0"),sQuery(id+"F21.wireOp",EDGE,"E108"),sQuery(id+"F21.wireOp",EDGE,"E109"),sQuery(id+"F21.wireOp",EDGE,"E112"),sQuery(id+"F21.wireOp",EDGE,"E113")])],"isStart":true});
            extrude(context, id + "F26", {"bodyType" : ToolBodyType.SURFACE, "surfaceEntities" : qUnion([Q0, Q1, Q2]), "endBound" : BoundingType.UP_TO_SURFACE, "endBoundEntityFace" : qUnion([Q3]), "depth" : 25 * mm});
        }
        {
            var Q0;
            Q0=makeQuery(id+"F18.opExtrude","CAP_FACE",FACE,{"disambiguationData":[OSD([sQuery(id+"F17.wireOp",EDGE,"E78.bottom"),sQuery(id+"F17.wireOp",EDGE,"E78.top"),sQuery(id+"F17.wireOp",EDGE,"E78.right"),sQuery(id+"F17.wireOp",EDGE,"E79"),sQuery(id+"F17.wireOp",EDGE,"E80"),sQuery(id+"F17.wireOp",EDGE,"E81.0"),sQuery(id+"F17.wireOp",EDGE,"E82"),sQuery(id+"F17.wireOp",EDGE,"E83")])],"isStart":false});
            var sketch = newSketch(context, id + "F27", { "sketchPlane" : qUnion([Q0])});
            skLineSegment(sketch, "E116.0", {"start": v(-960, 233.84) * mm, "end": v(-960, 0) * mm});
            skLineSegment(sketch, "E116.1", {"start": v(-960, 233.84) * mm, "end": v(-495.65, 336) * mm});
            skLineSegment(sketch, "E116.2", {"start": v(-495.65, 336) * mm, "end": v(0, 336) * mm});
            skSolve(sketch);
        }
        {
            var Q0;
            Q0=sQuery(id+"F27.wireOp",EDGE,"E116.0");
            var Q1;
            Q1=sQuery(id+"F27.wireOp",EDGE,"E116.1");
            var Q2;
            Q2=sQuery(id+"F27.wireOp",EDGE,"E116.2");
            var Q3;
            Q3=makeQuery(id+"F20.opExtrude","CAP_FACE",FACE,{"disambiguationData":[OSD([sQuery(id+"F19.wireOp",EDGE,"E86"),sQuery(id+"F19.wireOp",EDGE,"E87"),sQuery(id+"F19.wireOp",EDGE,"E90"),sQuery(id+"F19.wireOp",EDGE,"E91"),sQuery(id+"F19.wireOp",EDGE,"E93"),sQuery(id+"F19.wireOp",EDGE,"E94"),sQuery(id+"F19.wireOp",EDGE,"E95.0"),sQuery(id+"F19.wireOp",EDGE,"E96"),sQuery(id+"F19.wireOp",EDGE,"E97")])],"isStart":true});
            extrude(context, id + "F28", {"bodyType" : ToolBodyType.SURFACE, "surfaceEntities" : qUnion([Q0, Q1, Q2]), "endBound" : BoundingType.UP_TO_SURFACE, "endBoundEntityFace" : qUnion([Q3]), "depth" : 25 * mm});
        }
        {
            var Q0;
            Q0=makeQuery(id+"F9.opExtrude","SWEPT_FACE",FACE,{"disambiguationData":[OSD([sQuery(id+"F8.wireOp",EDGE,"E49.top")])]});
            var sketch = newSketch(context, id + "F29", { "sketchPlane" : qUnion([Q0])});
            skLineSegment(sketch, "E117.0", {"start": v(-910, 124) * mm, "end": v(-910, -86) * mm});
            skLineSegment(sketch, "E117.1", {"start": v(-910, 124) * mm, "end": v(-900, 124) * mm});
            skLineSegment(sketch, "E117.2", {"start": v(0, 124) * mm, "end": v(-900, 124) * mm});
            skSolve(sketch);
        }
        {
            var Q0;
            Q0=sQuery(id+"F29.wireOp",EDGE,"E117.0");
            var Q1;
            Q1=sQuery(id+"F29.wireOp",EDGE,"E117.1");
            var Q2;
            Q2=sQuery(id+"F29.wireOp",EDGE,"E117.2");
            var Q3;
            Q3=makeQuery(id+"F18.opExtrude","CAP_FACE",FACE,{"disambiguationData":[OSD([sQuery(id+"F17.wireOp",EDGE,"E78.bottom"),sQuery(id+"F17.wireOp",EDGE,"E78.top"),sQuery(id+"F17.wireOp",EDGE,"E78.right"),sQuery(id+"F17.wireOp",EDGE,"E79"),sQuery(id+"F17.wireOp",EDGE,"E80"),sQuery(id+"F17.wireOp",EDGE,"E81.0"),sQuery(id+"F17.wireOp",EDGE,"E82"),sQuery(id+"F17.wireOp",EDGE,"E83")])],"isStart":true});
            extrude(context, id + "F30", {"bodyType" : ToolBodyType.SURFACE, "surfaceEntities" : qUnion([Q0, Q1, Q2]), "endBound" : BoundingType.UP_TO_SURFACE, "endBoundEntityFace" : qUnion([Q3]), "depth" : 25 * mm});
        }
        {
            var Q0;
            Q0=makeQuery(id+"F9.opExtrude","SWEPT_FACE",FACE,{"disambiguationData":[OSD([sQuery(id+"F8.wireOp",EDGE,"E49.bottom")])]});
            var sketch = newSketch(context, id + "F31", { "sketchPlane" : qUnion([Q0])});
            skLineSegment(sketch, "E118.0", {"start": v(0, 86) * mm, "end": v(-900, 86) * mm});
            skSolve(sketch);
        }
        {
            var Q0;
            Q0=sQuery(id+"F31.wireOp",EDGE,"E118.0");
            var Q1;
            Q1=makeQuery(id+"F9.opExtrude","SWEPT_FACE",FACE,{"disambiguationData":[OSD([sQuery(id+"F8.wireOp",EDGE,"E47.top")])]});
            extrude(context, id + "F32", {"bodyType" : ToolBodyType.SURFACE, "surfaceEntities" : qUnion([Q0]), "endBound" : BoundingType.UP_TO_SURFACE, "endBoundEntityFace" : qUnion([Q1]), "depth" : 25 * mm});
        }
        {
            var Q0;
            Q0=makeQuery(id+"F10.opExtrude","SWEPT_EDGE",EDGE,{"disambiguationData":[OSD([sQuery(id+"F8.wireOp",EDGE,"E38.top"),sQuery(id+"F8.wireOp",EDGE,"E38.left")])]});
            var Q1;
            Q1=makeQuery(id+"F9.opExtrude","SWEPT_EDGE",EDGE,{"disambiguationData":[OSD([sQuery(id+"F8.wireOp",EDGE,"E38.top"),sQuery(id+"F8.wireOp",EDGE,"E38.left")])]});
            var Q2;
            Q2=makeQuery(id+"F10.opExtrude","SWEPT_EDGE",EDGE,{"disambiguationData":[OSD([sQuery(id+"F8.wireOp",EDGE,"E39.top"),sQuery(id+"F8.wireOp",EDGE,"E39.left")])]});
            var Q3;
            Q3=makeQuery(id+"F9.opExtrude","SWEPT_EDGE",EDGE,{"disambiguationData":[OSD([sQuery(id+"F8.wireOp",EDGE,"E39.top"),sQuery(id+"F8.wireOp",EDGE,"E39.left")])]});
            var Q4;
            Q4=makeQuery(id+"F10.opExtrude","SWEPT_EDGE",EDGE,{"disambiguationData":[OSD([sQuery(id+"F8.wireOp",EDGE,"E40.top"),sQuery(id+"F8.wireOp",EDGE,"E40.left")])]});
            var Q5;
            Q5=makeQuery(id+"F9.opExtrude","SWEPT_EDGE",EDGE,{"disambiguationData":[OSD([sQuery(id+"F8.wireOp",EDGE,"E40.top"),sQuery(id+"F8.wireOp",EDGE,"E40.left")])]});
            var Q6;
            Q6=makeQuery(id+"F10.opExtrude","SWEPT_EDGE",EDGE,{"disambiguationData":[OSD([sQuery(id+"F8.wireOp",EDGE,"E41.top"),sQuery(id+"F8.wireOp",EDGE,"E41.left")])]});
            var Q7;
            Q7=makeQuery(id+"F9.opExtrude","SWEPT_EDGE",EDGE,{"disambiguationData":[OSD([sQuery(id+"F8.wireOp",EDGE,"E41.top"),sQuery(id+"F8.wireOp",EDGE,"E41.left")])]});
            var Q8;
            Q8=makeQuery(id+"F10.opExtrude","SWEPT_EDGE",EDGE,{"disambiguationData":[OSD([sQuery(id+"F8.wireOp",EDGE,"E42.top"),sQuery(id+"F8.wireOp",EDGE,"E42.left")])]});
            var Q9;
            Q9=makeQuery(id+"F9.opExtrude","SWEPT_EDGE",EDGE,{"disambiguationData":[OSD([sQuery(id+"F8.wireOp",EDGE,"E42.top"),sQuery(id+"F8.wireOp",EDGE,"E42.left")])]});
            var Q10;
            Q10=makeQuery(id+"F10.opExtrude","SWEPT_EDGE",EDGE,{"disambiguationData":[OSD([sQuery(id+"F8.wireOp",EDGE,"E43.top"),sQuery(id+"F8.wireOp",EDGE,"E43.left")])]});
            var Q11;
            Q11=makeQuery(id+"F9.opExtrude","SWEPT_EDGE",EDGE,{"disambiguationData":[OSD([sQuery(id+"F8.wireOp",EDGE,"E43.top"),sQuery(id+"F8.wireOp",EDGE,"E43.left")])]});
            var Q12;
            Q12=makeQuery(id+"F10.opExtrude","SWEPT_EDGE",EDGE,{"disambiguationData":[OSD([sQuery(id+"F8.wireOp",EDGE,"E44.top"),sQuery(id+"F8.wireOp",EDGE,"E44.left")])]});
            var Q13;
            Q13=makeQuery(id+"F9.opExtrude","SWEPT_EDGE",EDGE,{"disambiguationData":[OSD([sQuery(id+"F8.wireOp",EDGE,"E44.top"),sQuery(id+"F8.wireOp",EDGE,"E44.left")])]});
            var Q14;
            Q14=makeQuery(id+"F10.opExtrude","SWEPT_EDGE",EDGE,{"disambiguationData":[OSD([sQuery(id+"F8.wireOp",EDGE,"E45.top"),sQuery(id+"F8.wireOp",EDGE,"E45.left")])]});
            var Q15;
            Q15=makeQuery(id+"F9.opExtrude","SWEPT_EDGE",EDGE,{"disambiguationData":[OSD([sQuery(id+"F8.wireOp",EDGE,"E45.top"),sQuery(id+"F8.wireOp",EDGE,"E45.left")])]});
            var Q16;
            Q16=makeQuery(id+"F10.opExtrude","SWEPT_EDGE",EDGE,{"disambiguationData":[OSD([sQuery(id+"F8.wireOp",EDGE,"E46.top"),sQuery(id+"F8.wireOp",EDGE,"E46.left")])]});
            var Q17;
            Q17=makeQuery(id+"F9.opExtrude","SWEPT_EDGE",EDGE,{"disambiguationData":[OSD([sQuery(id+"F8.wireOp",EDGE,"E46.top"),sQuery(id+"F8.wireOp",EDGE,"E46.left")])]});
            var Q18;
            Q18=makeQuery(id+"F9.opExtrude","SWEPT_EDGE",EDGE,{"disambiguationData":[OSD([sQuery(id+"F8.wireOp",EDGE,"E47.top"),sQuery(id+"F8.wireOp",EDGE,"E47.left")])]});
            var Q19;
            {var subQ0=sQuery(id+"F8.wireOp",EDGE,"E49.left");var subQ1=sQuery(id+"F8.wireOp",EDGE,"E49.top");Q19=makeQuery(id+"F13.boolean.opBoolean","MERGE",EDGE,{"derivedFrom":[makeQuery(id+"F9.opExtrude","SWEPT_EDGE",EDGE,{"disambiguationData":[OSD([subQ1,subQ0])]}),makeQuery(id+"F13.opExtrude","SWEPT_EDGE",EDGE,{"disambiguationData":[OSD([subQ1,subQ0])]})]});}
            var Q20;
            Q20=makeQuery(id+"F13.opExtrude","CAP_EDGE",EDGE,{"disambiguationData":[OSD([sQuery(id+"F8.wireOp",EDGE,"E49.top")])],"isStart":false});
            var Q21;
            Q21=makeQuery(id+"F18.opExtrude","CAP_EDGE",EDGE,{"disambiguationData":[OSD([sQuery(id+"F17.wireOp",EDGE,"E79"),sQuery(id+"F17.wireOp",EDGE,"E83")])],"isStart":false});
            var Q22;
            Q22=makeQuery(id+"F18.opExtrude","CAP_EDGE",EDGE,{"disambiguationData":[OSD([sQuery(id+"F17.wireOp",EDGE,"E80")])],"isStart":false});
            var Q23;
            Q23=makeQuery(id+"F18.opExtrude","CAP_EDGE",EDGE,{"disambiguationData":[OSD([sQuery(id+"F17.wireOp",EDGE,"E78.bottom")])],"isStart":false});
            var Q24;
            Q24=makeQuery(id+"F20.opExtrude","CAP_EDGE",EDGE,{"disambiguationData":[OSD([sQuery(id+"F19.wireOp",EDGE,"E93"),sQuery(id+"F19.wireOp",EDGE,"E97")])],"isStart":false});
            var Q25;
            Q25=makeQuery(id+"F20.opExtrude","CAP_EDGE",EDGE,{"disambiguationData":[OSD([sQuery(id+"F19.wireOp",EDGE,"E94")])],"isStart":false});
            var Q26;
            Q26=makeQuery(id+"F20.opExtrude","CAP_EDGE",EDGE,{"disambiguationData":[OSD([sQuery(id+"F19.wireOp",EDGE,"E86")])],"isStart":false});
            var Q27;
            Q27=makeQuery(id+"F22.opExtrude","CAP_EDGE",EDGE,{"disambiguationData":[OSD([sQuery(id+"F21.wireOp",EDGE,"E109"),sQuery(id+"F21.wireOp",EDGE,"E112")])],"isStart":false});
            var Q28;
            Q28=makeQuery(id+"F22.opExtrude","CAP_EDGE",EDGE,{"disambiguationData":[OSD([sQuery(id+"F21.wireOp",EDGE,"E113")])],"isStart":false});
            var Q29;
            Q29=makeQuery(id+"F22.opExtrude","CAP_EDGE",EDGE,{"disambiguationData":[OSD([sQuery(id+"F21.wireOp",EDGE,"E100")])],"isStart":false});
            chamfer(context, id + "F33", {"entities" : qUnion([Q0, Q1, Q2, Q3, Q4, Q5, Q6, Q7, Q8, Q9, Q10, Q11, Q12, Q13, Q14, Q15, Q16, Q17, Q18, Q19, Q20, Q21, Q22, Q23, Q24, Q25, Q26, Q27, Q28, Q29]), "width" : 10 * mm, "tangentPropagation" : true});
        }
    });
